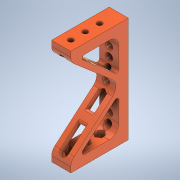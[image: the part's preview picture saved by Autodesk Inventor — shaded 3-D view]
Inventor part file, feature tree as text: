
AUTODESK INVENTOR PART (.ipt)
format: ipt  version: 2020 (Build 240168000, 168)  size: 476,672 bytes
history: native  units: in
note: dims shown in document units (in); Inventor stores cm internally (conversion verified against a paired STEP export)
features: extrude x10, sketch x10, plane x4, fillet x2, mirror x1
ambient origin geometry x8: Origin, YZ Plane, XZ Plane, XY Plane, X Axis, Y Axis, Z Axis, Center Point
bodies: Solid1 (feature_tree)
feature tree (27):
  extrude  "Extrusion1"  Depth=5.5in
  extrude  "Extrusion2"  Depth=0.5in
  fillet  "Fillet1"  Radius=0.5in
  extrude  "Extrusion3"  Depth=0.25in
  fillet  "Fillet2"  Radius=0.25in
  extrude  "Extrusion4"  Depth=0.5in
  plane  "Work Plane1"
  extrude  "Extrusion5"  Depth=0.125in
  extrude  "Extrusion6"  Depth=0.3937in
  plane  "Work Plane2"
  extrude  "Extrusion7"  [1 undecoded]
  plane  "Work Plane3"
  extrude  "Extrusion8"  Depth=0.3937in
  extrude  "Extrusion9"  Depth=0.25in
  extrude  "Extrusion10"  Depth=0.26in
  plane  "Work Plane4"
  mirror  "Mirror1"
  sketch  "Sketch1"  dims[d0=1.0in d1=5.5in]
  sketch  "Sketch2"  dims[d2=3.0in d3=0.0in d4=0.5in d5=0.5in]
  sketch  "Sketch3"  dims[d6=0.0in d7=0.0in d8=0.5in d9=0.25in]
  sketch  "Sketch4"  dims[d10=1.0in d11=0.0in d12=0.5in]
  sketch  "Sketch5"  dims[d13=0.125in d14=0.2in]
  sketch  "Sketch6"  dims[d16=2.5in d17=4.3307in d19=0.5in d20=0.3937in d22=1.0in]
  sketch  "Sketch7"  dims[d24=0.0in d25=0.0in d26=-0.25in]
  sketch  "Sketch8"  dims[d27=0.375in d28=3.5433in d30=0.5in d31=0.3937in d33=1.0in]
  sketch  "Sketch9"  dims[d35=0.25in d36=0.0in d37=1.0in]
  sketch  "Sketch10"  dims[d38=0.5in d39=0.2656in d40=1.1811in d42=0.75in d43=0.3937in d45=1.0in d47=0.0in d48=0.0in d49=-0.25in d50=0.4375in d51=2.5in d52=0.0in d53=-0.25in d54=0.4375in d55=2.5in d56=0.0in d57=0.26in d58=0.0in d59=0.375in d60=0.26in d61=0.0in d62=0.5in d63=0.0344in d64=0.5in d65=0.0344in]
note: 1 required parameter value undecoded (feature->parameter linkage not recoverable at this tier; creation-order binding heuristic only, values carry confidence <= 0.55)
